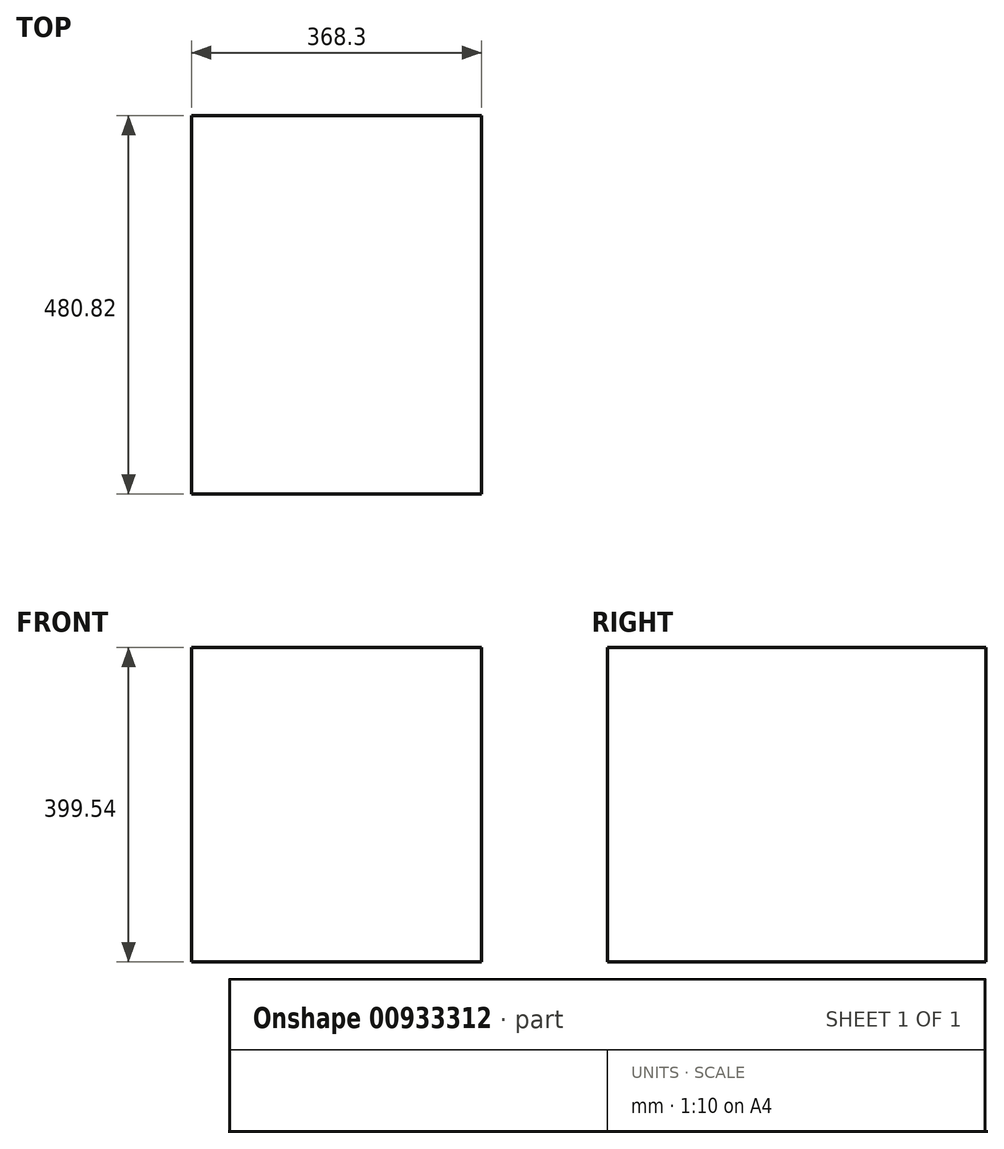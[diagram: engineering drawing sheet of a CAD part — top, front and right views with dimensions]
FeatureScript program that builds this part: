
annotation { "Feature Type Name" : "Feature", "Feature Type Description" : "" }
export const myFeature = defineFeature(function(context is Context, id is Id, definition is map)
    precondition{}
    {
        {
            var Q0;
            Q0=qCreatedBy(makeId("Front.planeOp"),FACE);
            var sketch = newSketch(context, id + "F0", { "sketchPlane" : qUnion([Q0])});
            skLineSegment(sketch, "E0.bottom", {"start": v(0, 0) * mm, "end": v(368.3, 0) * mm});
            skLineSegment(sketch, "E0.top", {"start": v(0, 399.54) * mm, "end": v(368.3, 399.54) * mm});
            skLineSegment(sketch, "E0.left", {"start": v(0, 0) * mm, "end": v(0, 399.54) * mm});
            skLineSegment(sketch, "E0.right", {"start": v(368.3, 0) * mm, "end": v(368.3, 399.54) * mm});
            skSolve(sketch);
        }
        {
            var Q0;
            Q0=makeQuery(id+"F0.imprint","IMPRINT",FACE,{"disambiguationData":[TD([[makeQuery(id+"F0.imprint","IMPRINT",EDGE,{"derivedFrom":sQuery(id+"F0.wireOp",EDGE,"E0.bottom")}),1.0]])]});
            extrude(context, id + "F1", {"entities" : qUnion([Q0]), "depth" : 480.82 * mm, "offsetDistance" : 25.4 * mm});
        }
    });
